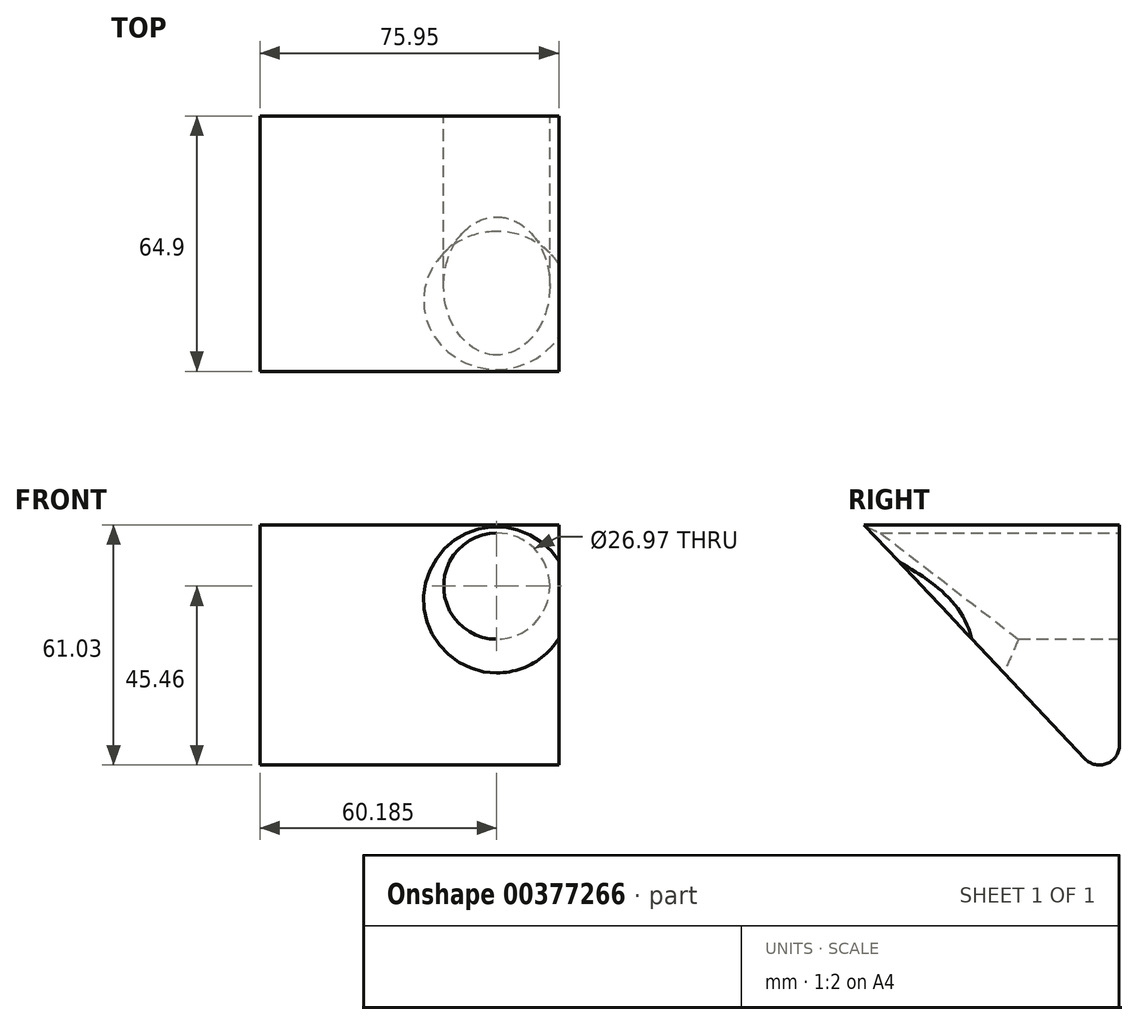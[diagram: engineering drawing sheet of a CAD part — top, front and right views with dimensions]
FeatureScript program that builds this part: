
annotation { "Feature Type Name" : "Feature", "Feature Type Description" : "" }
export const myFeature = defineFeature(function(context is Context, id is Id, definition is map)
    precondition{}
    {
        {
            var Q0;
            Q0=qCreatedBy(makeId("Right.planeOp"),FACE);
            var sketch = newSketch(context, id + "F0", { "sketchPlane" : qUnion([Q0])});
            skLineSegment(sketch, "E0", {"start": v(-48.57, 49.23) * mm, "end": v(16.33, 49.23) * mm});
            skLineSegment(sketch, "E1", {"start": v(16.33, 49.23) * mm, "end": v(16.33, -19.5) * mm});
            skLineSegment(sketch, "E2", {"start": v(16.33, -19.5) * mm, "end": v(-48.57, 49.23) * mm});
            skSolve(sketch);
        }
        {
            var Q0;
            Q0=makeQuery(id+"F0.imprint","IMPRINT",FACE,{"disambiguationData":[TD([[makeQuery(id+"F0.imprint","IMPRINT",EDGE,{"derivedFrom":sQuery(id+"F0.wireOp",EDGE,"E0")}),-1.0]])]});
            extrude(context, id + "F1", {"entities" : qUnion([Q0]), "depth" : 75.95 * mm});
        }
        {
            var Q0;
            Q0=makeQuery(id+"F1.opExtrude","SWEPT_FACE",FACE,{"disambiguationData":[OSD([sQuery(id+"F0.wireOp",EDGE,"E1")])]});
            var sketch = newSketch(context, id + "F2", { "sketchPlane" : qUnion([Q0])});
            skCircle(sketch, "E3", {"center": v(-60.18, 33.66) * mm, "radius": 13.49 * mm});
            skSolve(sketch);
        }
        {
            var Q0;
            Q0=makeQuery(id+"F2.imprint","IMPRINT",FACE,{"disambiguationData":[TD([[makeQuery(id+"F2.imprint","IMPRINT",EDGE,{"derivedFrom":sQuery(id+"F2.wireOp",EDGE,"E3")}),1.0]])]});
            extrude(context, id + "F3", {"entities" : qUnion([Q0]), "operationType" : NewBodyOperationType.REMOVE, "oppositeDirection" : true, "depth" : 75.95 * mm});
        }
        {
            var Q0;
            Q0=makeQuery(id+"F1.opExtrude","SWEPT_EDGE",EDGE,{"disambiguationData":[OSD([sQuery(id+"F0.wireOp",EDGE,"E1"),sQuery(id+"F0.wireOp",EDGE,"E2")])]});
            fillet(context, id + "F4", {"entities" : qUnion([Q0]), "radius" : 5.08 * mm, "tangentPropagation" : true, "allowEdgeOverflow" : false});
        }
        {
            var Q0;
            Q0=makeQuery(id+"F3.boolean.opBoolean","INTERSECT",EDGE,{"derivedFrom":[makeQuery(id+"F1.opExtrude","SWEPT_FACE",FACE,{"disambiguationData":[OSD([sQuery(id+"F0.wireOp",EDGE,"E2")])]}),makeQuery(id+"F3.opExtrude","SWEPT_FACE",FACE,{"disambiguationData":[OSD([sQuery(id+"F2.wireOp",EDGE,"E3")])]})]});
            chamfer(context, id + "F5", {"entities" : qUnion([Q0]), "width" : 5.08 * mm, "tangentPropagation" : true});
        }
    });
